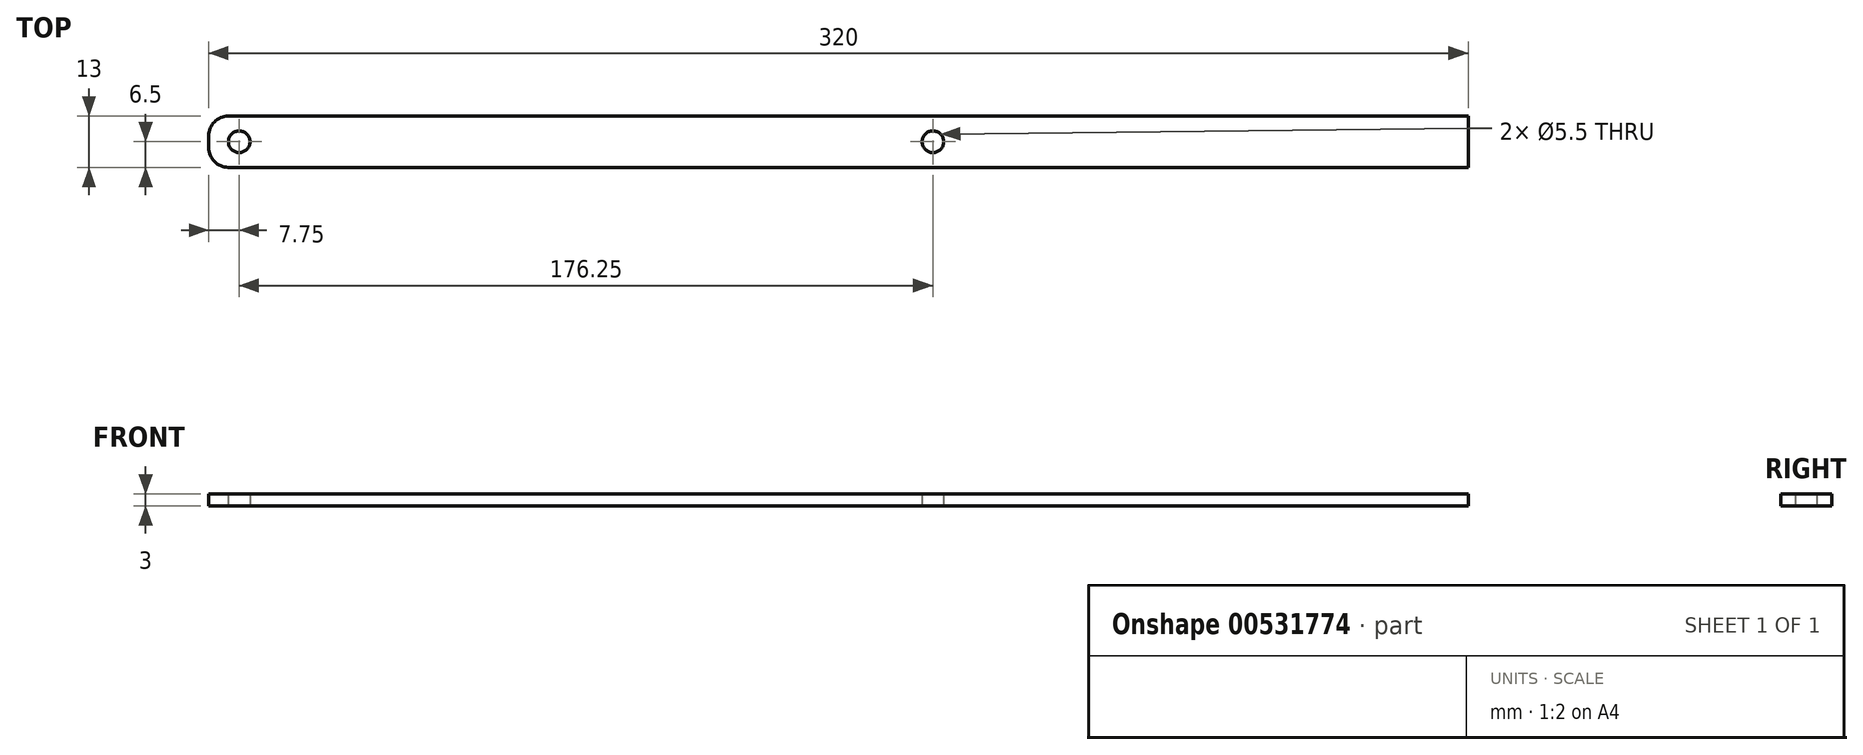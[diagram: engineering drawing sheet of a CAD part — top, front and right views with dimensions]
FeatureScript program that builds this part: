
annotation { "Feature Type Name" : "Feature", "Feature Type Description" : "" }
export const myFeature = defineFeature(function(context is Context, id is Id, definition is map)
    precondition{}
    {
        {
            var Q0;
            Q0=qCreatedBy(makeId("Top.planeOp"),FACE);
            var sketch = newSketch(context, id + "F0", { "sketchPlane" : qUnion([Q0])});
            skLineSegment(sketch, "E0.bottom", {"start": v(160, -6.5) * mm, "end": v(-155, -6.5) * mm});
            skLineSegment(sketch, "E0.top", {"start": v(160, 6.5) * mm, "end": v(-155, 6.5) * mm});
            skLineSegment(sketch, "E0.left", {"start": v(160, -6.5) * mm, "end": v(160, 6.5) * mm});
            skLineSegment(sketch, "E0.right", {"start": v(-160, -1.5) * mm, "end": v(-160, 1.5) * mm});
            skPoint(sketch, "E0.middle", {"position": v(0, 0) * mm});
            skCircle(sketch, "E1", {"center": v(-152.25, 0) * mm, "radius": 2.75 * mm});
            skCircle(sketch, "E2", {"center": v(24, 0) * mm, "radius": 2.75 * mm});
            skPoint(sketch, "E3.visualSharp", {"position": v(-160, 6.5) * mm});
            skArc(sketch, "E3.filletArc", {"start": v(-155, 6.5) * mm, "mid": v(-158.54, 5.04) * mm, "end": v(-160, 1.5) * mm});
            skPoint(sketch, "E4.visualSharp", {"position": v(-160, -6.5) * mm});
            skArc(sketch, "E4.filletArc", {"start": v(-160, -1.5) * mm, "mid": v(-158.54, -5.04) * mm, "end": v(-155, -6.5) * mm});
            skSolve(sketch);
        }
        {
            var Q0;
            Q0=makeQuery(id+"F0.imprint","IMPRINT",FACE,{"disambiguationData":[TD([[makeQuery(id+"F0.imprint","IMPRINT",EDGE,{"derivedFrom":sQuery(id+"F0.wireOp",EDGE,"E0.bottom")}),-1.0]])]});
            extrude(context, id + "F1", {"entities" : qUnion([Q0]), "depth" : 3 * mm, "offsetDistance" : 25 * mm});
        }
    });
